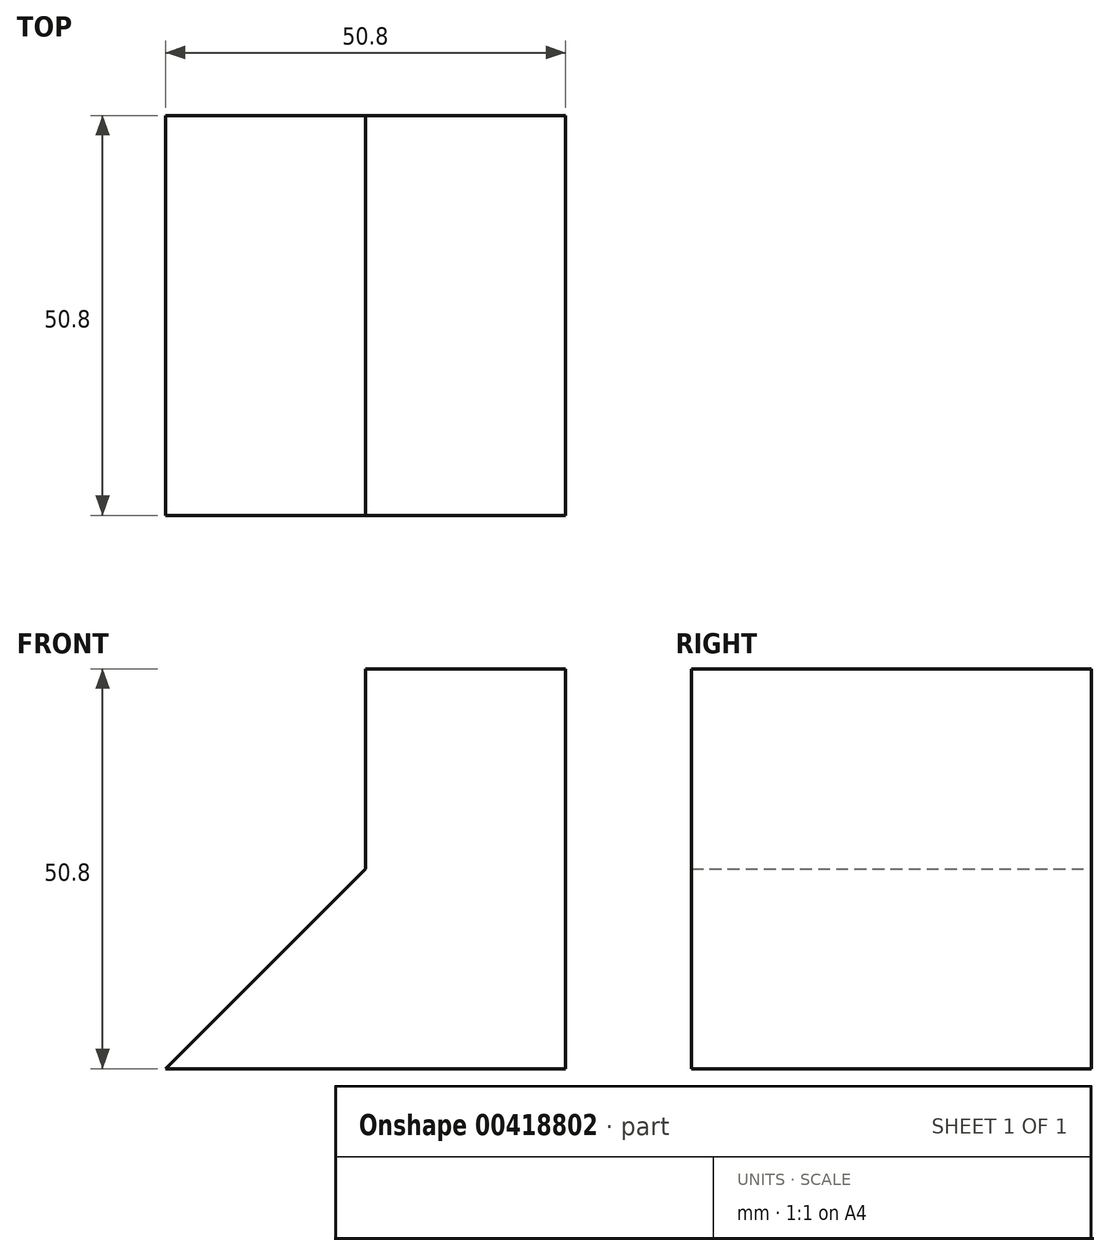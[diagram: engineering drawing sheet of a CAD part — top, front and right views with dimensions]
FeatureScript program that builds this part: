
annotation { "Feature Type Name" : "Feature", "Feature Type Description" : "" }
export const myFeature = defineFeature(function(context is Context, id is Id, definition is map)
    precondition{}
    {
        {
            var Q0;
            Q0=qCreatedBy(makeId("Front.planeOp"),FACE);
            var sketch = newSketch(context, id + "F0", { "sketchPlane" : qUnion([Q0])});
            skLineSegment(sketch, "E0", {"start": v(-52.9, 0) * mm, "end": v(-2.1, 0) * mm});
            skLineSegment(sketch, "E1", {"start": v(-2.1, 0) * mm, "end": v(-2.1, 50.8) * mm});
            skLineSegment(sketch, "E2", {"start": v(-2.1, 50.8) * mm, "end": v(-27.5, 50.8) * mm});
            skLineSegment(sketch, "E3", {"start": v(-27.5, 50.8) * mm, "end": v(-27.5, 25.4) * mm});
            skLineSegment(sketch, "E4", {"start": v(-27.5, 25.4) * mm, "end": v(-52.9, 0) * mm});
            skSolve(sketch);
        }
        {
            var Q0;
            Q0=makeQuery(id+"F0.imprint","IMPRINT",FACE,{"disambiguationData":[TD([[makeQuery(id+"F0.imprint","IMPRINT",EDGE,{"derivedFrom":sQuery(id+"F0.wireOp",EDGE,"E0")}),1.0]])]});
            extrude(context, id + "F1", {"entities" : qUnion([Q0]), "depth" : 50.8 * mm});
        }
    });
